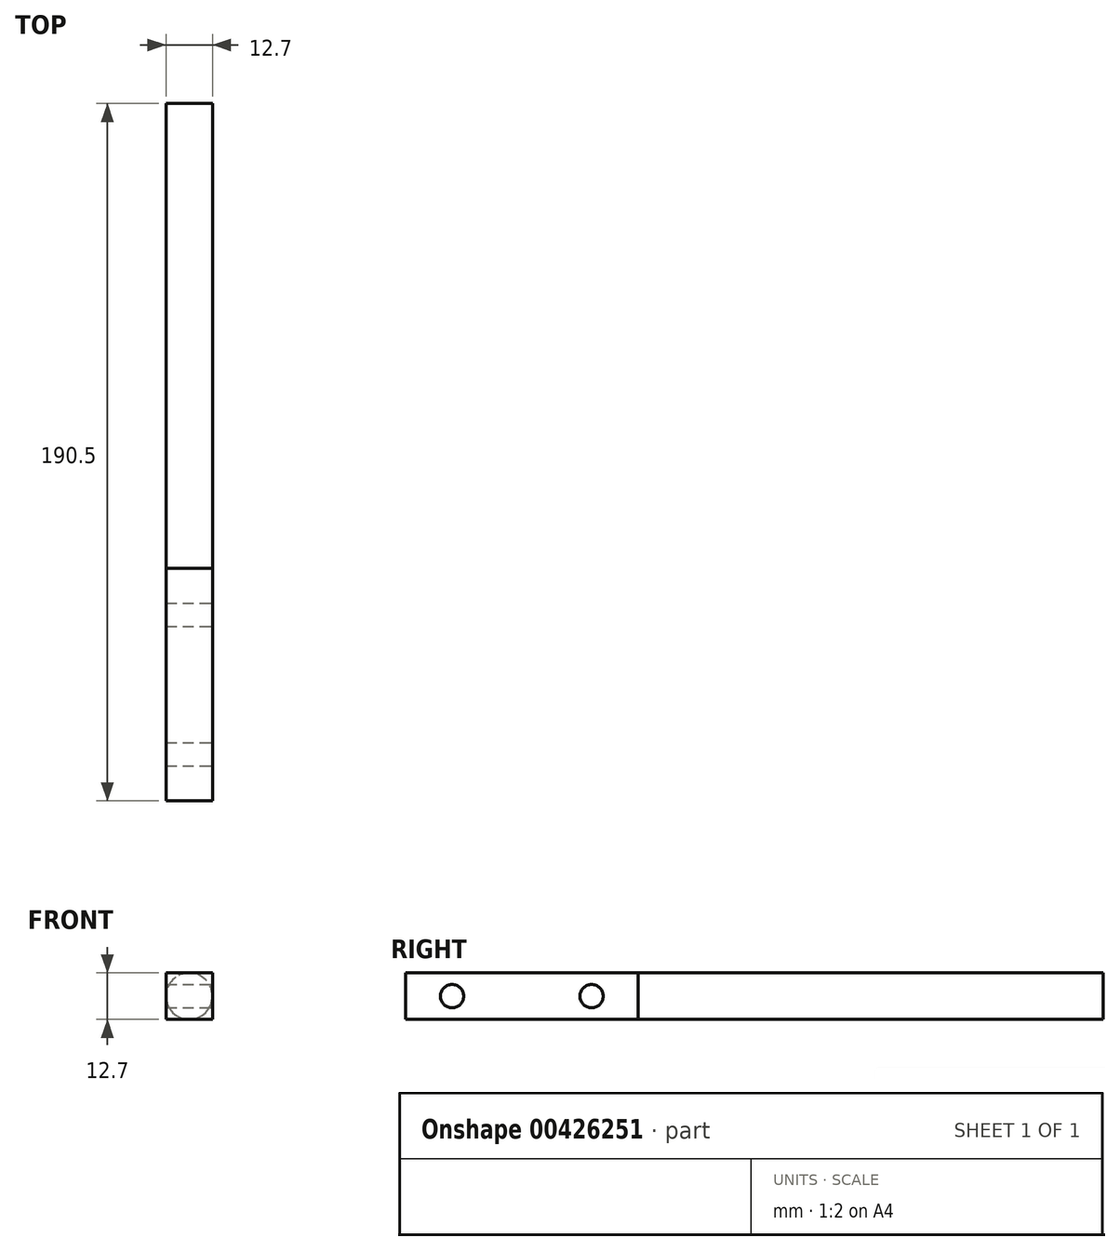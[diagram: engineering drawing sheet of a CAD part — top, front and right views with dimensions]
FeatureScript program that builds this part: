
annotation { "Feature Type Name" : "Feature", "Feature Type Description" : "" }
export const myFeature = defineFeature(function(context is Context, id is Id, definition is map)
    precondition{}
    {
        {
            var Q0;
            Q0=qCreatedBy(makeId("Front.planeOp"),FACE);
            var sketch = newSketch(context, id + "F0", { "sketchPlane" : qUnion([Q0])});
            skCircle(sketch, "E0", {"center": v(0, 0) * mm, "radius": 6.35 * mm});
            skSolve(sketch);
        }
        {
            var Q0;
            Q0 = qSketchRegion(id + "F0", true);
            extrude(context, id + "F1", {"entities" : qUnion([Q0]), "depth" : 127 * mm});
        }
        {
            var Q0;
            Q0=makeQuery(id+"F1.opExtrude","CAP_FACE",FACE,{"disambiguationData":[OSD([sQuery(id+"F0.wireOp",EDGE,"E0")])],"isStart":false});
            var sketch = newSketch(context, id + "F2", { "sketchPlane" : qUnion([Q0])});
            skLineSegment(sketch, "E1", {"start": v(6.35, 6.35) * mm, "end": v(-6.35, 6.35) * mm});
            skLineSegment(sketch, "E2", {"start": v(-6.35, 6.35) * mm, "end": v(-6.35, -6.35) * mm});
            skLineSegment(sketch, "E3", {"start": v(6.35, -6.35) * mm, "end": v(-6.35, -6.35) * mm});
            skLineSegment(sketch, "E4", {"start": v(6.35, 6.35) * mm, "end": v(6.35, -6.35) * mm});
            skSolve(sketch);
        }
        {
            var Q0;
            Q0 = qSketchRegion(id + "F2", true);
            extrude(context, id + "F3", {"entities" : qUnion([Q0]), "operationType" : NewBodyOperationType.ADD, "depth" : 63.5 * mm});
        }
        {
            var Q0;
            Q0=makeQuery(id+"F3.opExtrude","SWEPT_FACE",FACE,{"disambiguationData":[OSD([sQuery(id+"F2.wireOp",EDGE,"E4")])]});
            var sketch = newSketch(context, id + "F4", { "sketchPlane" : qUnion([Q0])});
            skCircle(sketch, "E5", {"center": v(-177.8, 0) * mm, "radius": 3.18 * mm});
            skCircle(sketch, "E6", {"center": v(-139.7, 0) * mm, "radius": 3.18 * mm});
            skSolve(sketch);
        }
        {
            var Q0;
            Q0 = qSketchRegion(id + "F4", true);
            extrude(context, id + "F5", {"entities" : qUnion([Q0]), "operationType" : NewBodyOperationType.REMOVE, "endBound" : BoundingType.THROUGH_ALL, "oppositeDirection" : true, "depth" : 25.4 * mm});
        }
    });
